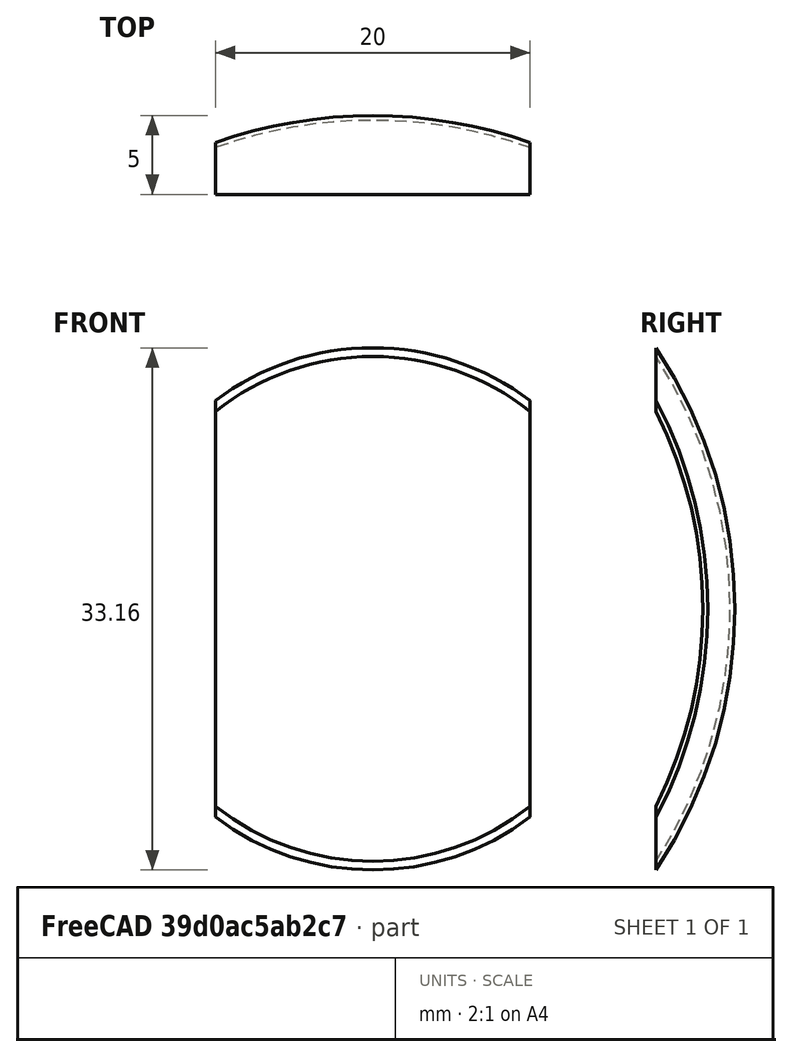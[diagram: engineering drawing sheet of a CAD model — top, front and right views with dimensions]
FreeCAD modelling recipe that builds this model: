
FCSTD DOCUMENT  (FreeCAD 0.21R33771 (Git))
Label: subtractive-sphere-cut-1
License: All rights reserved
LicenseURL: https://en.wikipedia.org/wiki/All_rights_reserved
objects: Part::Cut×4, Part::Box×3, Part::Sphere×2
note: 9 computed .brp shape members not serialized (recipe doc carries the construction recipe); baked Part::Feature solids carry a one-line shape summary decoded from their .brp

FEATURE [Part::Sphere] Sphere  label="Outer"
  Angle1 = -90
  Angle2 = 90
  Angle3 = 180
  AttacherType = Attacher::AttachEngine3D
  Radius = 30
FEATURE [Part::Sphere] Sphere001  label="Inner"
  Angle1 = -90
  Angle2 = 90
  Angle3 = 180
  AttacherType = Attacher::AttachEngine3D
  Radius = 29.7
FEATURE [Part::Cut] Cut
  Base = -> Sphere
  Tool = -> Sphere001
FEATURE [Part::Box] Box  label="Cube"
  AttacherType = Attacher::AttachEngine3D
  Height = 60
  Length = 60
  Placement = pos=(-30,-15,-30) rot=(0,0,1;0rad)
  Width = 40
FEATURE [Part::Cut] Cut001  label="ThinMirror"
  Base = -> Cut
  Tool = -> Box
FEATURE [Part::Box] Box001  label="Cube001"
  AttacherType = Attacher::AttachEngine3D
  Height = 40
  Length = 10
  Placement = pos=(10,20,-20) rot=(0,0,1;0rad)
  Width = 10
FEATURE [Part::Box] Box002  label="Cube002"
  AttacherType = Attacher::AttachEngine3D
  Height = 40
  Length = 10
  Placement = pos=(-20,20,-20) rot=(0,0,1;0rad)
  Width = 10
FEATURE [Part::Cut] Cut002
  Base = -> Cut001
  Tool = -> Box001
FEATURE [Part::Cut] Cut003  label="CutMirror"
  Base = -> Cut002
  Tool = -> Box002
